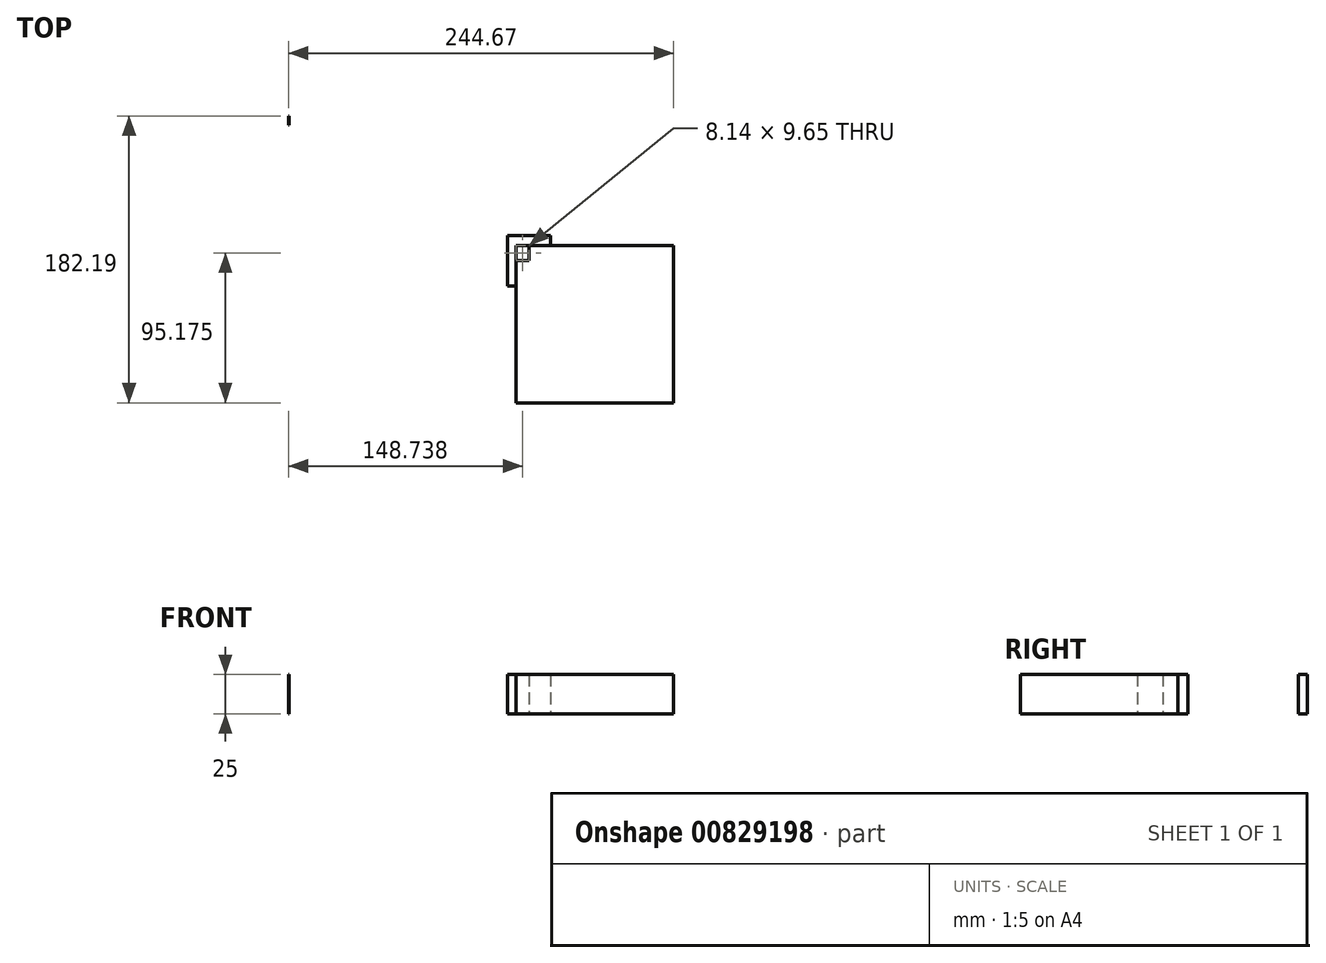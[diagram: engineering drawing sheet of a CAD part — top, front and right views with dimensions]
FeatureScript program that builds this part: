
annotation { "Feature Type Name" : "Feature", "Feature Type Description" : "" }
export const myFeature = defineFeature(function(context is Context, id is Id, definition is map)
    precondition{}
    {
        {
            var Q0;
            Q0=qCreatedBy(makeId("Top.planeOp"),FACE);
            var sketch = newSketch(context, id + "F0", { "sketchPlane" : qUnion([Q0])});
            skLineSegment(sketch, "E0.bottom", {"start": v(-50, 50) * mm, "end": v(50, 50) * mm});
            skLineSegment(sketch, "E0.top", {"start": v(-50, -50) * mm, "end": v(50, -50) * mm});
            skLineSegment(sketch, "E0.left", {"start": v(-50, 50) * mm, "end": v(-50, -50) * mm});
            skLineSegment(sketch, "E0.right", {"start": v(50, 50) * mm, "end": v(50, -50) * mm});
            skPoint(sketch, "E0.middle", {"position": v(0, 0) * mm});
            skSolve(sketch);
        }
        {
            var Q0;
            Q0=makeQuery(id+"F0.imprint","IMPRINT",FACE,{"disambiguationData":[TD([[makeQuery(id+"F0.imprint","IMPRINT",EDGE,{"derivedFrom":sQuery(id+"F0.wireOp",EDGE,"E0.bottom")}),-1.0]])]});
            var sketch = newSketch(context, id + "F1", { "sketchPlane" : qUnion([Q0])});
            skSolve(sketch);
        }
        {
            var Q0;
            Q0=makeQuery(id+"F0.imprint","IMPRINT",FACE,{"disambiguationData":[TD([[makeQuery(id+"F0.imprint","IMPRINT",EDGE,{"derivedFrom":sQuery(id+"F0.wireOp",EDGE,"E0.bottom")}),-1.0]])]});
            var sketch = newSketch(context, id + "F2", { "sketchPlane" : qUnion([Q0])});
            skLineSegment(sketch, "E1.bottom", {"start": v(-194.32, 126.39) * mm, "end": v(-194.67, 126.39) * mm});
            skLineSegment(sketch, "E1.top", {"start": v(-194.32, 132.19) * mm, "end": v(-194.67, 132.19) * mm});
            skLineSegment(sketch, "E1.left", {"start": v(-194.32, 126.39) * mm, "end": v(-194.32, 132.19) * mm});
            skLineSegment(sketch, "E1.right", {"start": v(-194.67, 126.39) * mm, "end": v(-194.67, 132.19) * mm});
            skPoint(sketch, "E1.middle", {"position": v(-194.5, 129.29) * mm});
            skLineSegment(sketch, "E2.bottom", {"start": v(-41.86, 40.35) * mm, "end": v(-55.64, 40.35) * mm});
            skLineSegment(sketch, "E2.top", {"start": v(-41.86, 56.4) * mm, "end": v(-55.64, 56.4) * mm});
            skLineSegment(sketch, "E2.left", {"start": v(-41.86, 40.35) * mm, "end": v(-41.86, 56.4) * mm});
            skLineSegment(sketch, "E2.right", {"start": v(-55.64, 40.35) * mm, "end": v(-55.64, 56.4) * mm});
            skPoint(sketch, "E2.middle", {"position": v(-48.75, 48.38) * mm});
            skLineSegment(sketch, "E3.bottom", {"start": v(-55.64, 56.4) * mm, "end": v(-28.1, 56.4) * mm});
            skLineSegment(sketch, "E3.top", {"start": v(-55.64, 24.3) * mm, "end": v(-28.1, 24.3) * mm});
            skLineSegment(sketch, "E3.left", {"start": v(-55.64, 56.4) * mm, "end": v(-55.64, 24.3) * mm});
            skLineSegment(sketch, "E3.right", {"start": v(-28.1, 56.4) * mm, "end": v(-28.1, 24.3) * mm});
            skPoint(sketch, "E3.middle", {"position": v(-41.86, 40.35) * mm});
            skLineSegment(sketch, "E4.bottom", {"start": v(50, -50) * mm, "end": v(-50, -50) * mm});
            skLineSegment(sketch, "E4.top", {"start": v(50, 50) * mm, "end": v(-50, 50) * mm});
            skLineSegment(sketch, "E4.left", {"start": v(50, -50) * mm, "end": v(50, 50) * mm});
            skLineSegment(sketch, "E4.right", {"start": v(-50, -50) * mm, "end": v(-50, 50) * mm});
            skPoint(sketch, "E4.middle", {"position": v(0, 0) * mm});
            skSolve(sketch);
        }
        {
            var Q0;
            Q0=makeQuery(id+"F2.imprint","IMPRINT",FACE,{"disambiguationData":[TD([[makeQuery(id+"F2.imprint","IMPRINT",EDGE,{"derivedFrom":sQuery(id+"F2.wireOp",EDGE,"E1.bottom")}),-1.0]])]});
            var Q1;
            {var subQ6=sQuery(id+"F2.wireOp",EDGE,"E4.bottom");Q1=makeQuery(id+"F2.imprint","IMPRINT",FACE,{"disambiguationData":[TD([[makeQuery(id+"F2.imprint","IMPRINT",EDGE,{"derivedFrom":subQ6}),1.0]])]});}
            var Q2;
            {var subQ0=sQuery(id+"F2.wireOp",EDGE,"E3.left");var subQ1=sQuery(id+"F2.wireOp",EDGE,"E2.bottom");var subQ2=makeQuery(id+"F2.imprint","INTERSECT",VERTEX,{"derivedFrom":[subQ1,subQ0]});Q2=makeQuery(id+"F2.imprint","IMPRINT",FACE,{"disambiguationData":[TD([[makeQuery(id+"F2.imprint","IMPRINT",EDGE,{"disambiguationData":[TD([[subQ2,1.0]])],"derivedFrom":subQ1}),1.0]])]});}
            var Q3;
            {var subQ0=sQuery(id+"F2.wireOp",EDGE,"E3.bottom");var subQ1=sQuery(id+"F2.wireOp",EDGE,"E2.left");var subQ2=makeQuery(id+"F2.imprint","INTERSECT",VERTEX,{"derivedFrom":[subQ1,subQ0]});Q3=makeQuery(id+"F2.imprint","IMPRINT",FACE,{"disambiguationData":[TD([[makeQuery(id+"F2.imprint","IMPRINT",EDGE,{"disambiguationData":[TD([[subQ2,1.0]])],"derivedFrom":subQ1}),-1.0]])]});}
            var Q4;
            {var subQ3=sQuery(id+"F2.wireOp",EDGE,"E3.left");var subQ5=sQuery(id+"F2.wireOp",EDGE,"E2.bottom");var subQ6=makeQuery(id+"F2.imprint","INTERSECT",VERTEX,{"derivedFrom":[subQ5,subQ3]});Q4=makeQuery(id+"F2.imprint","IMPRINT",FACE,{"disambiguationData":[TD([[makeQuery(id+"F2.imprint","IMPRINT",EDGE,{"disambiguationData":[TD([[subQ6,1.0]])],"derivedFrom":subQ5}),-1.0]])]});}
            var Q5;
            {var subQ5=sQuery(id+"F2.wireOp",EDGE,"E2.left");var subQ6=sQuery(id+"F2.wireOp",EDGE,"E2.bottom");var subQ7=makeQuery(id+"F2.imprint","INTERSECT",VERTEX,{"derivedFrom":[subQ6,subQ5]});Q5=makeQuery(id+"F2.imprint","IMPRINT",FACE,{"disambiguationData":[TD([[makeQuery(id+"F2.imprint","IMPRINT",EDGE,{"disambiguationData":[TD([[subQ7,-1.0]])],"derivedFrom":subQ6}),1.0]])]});}
            var Q6;
            Q6=makeQuery(id+"F0.imprint","IMPRINT",FACE,{"disambiguationData":[TD([[makeQuery(id+"F0.imprint","IMPRINT",EDGE,{"derivedFrom":sQuery(id+"F0.wireOp",EDGE,"E0.bottom")}),-1.0]])]});
            var Q7;
            Q7=makeQuery(id+"F1.imprint","IMPRINT",FACE,{"disambiguationData":[TD([[makeQuery(id+"F1.imprint","IMPRINT",EDGE,{"derivedFrom":makeQuery(id+"F0.imprint","IMPRINT",EDGE,{"derivedFrom":sQuery(id+"F0.wireOp",EDGE,"E0.bottom")})}),-1.0]])]});
            extrude(context, id + "F3", {"entities" : qUnion([Q0, Q1, Q2, Q3, Q4, Q5, Q6, Q7]), "depth" : 25 * mm, "offsetDistance" : 25 * mm});
        }
    });
